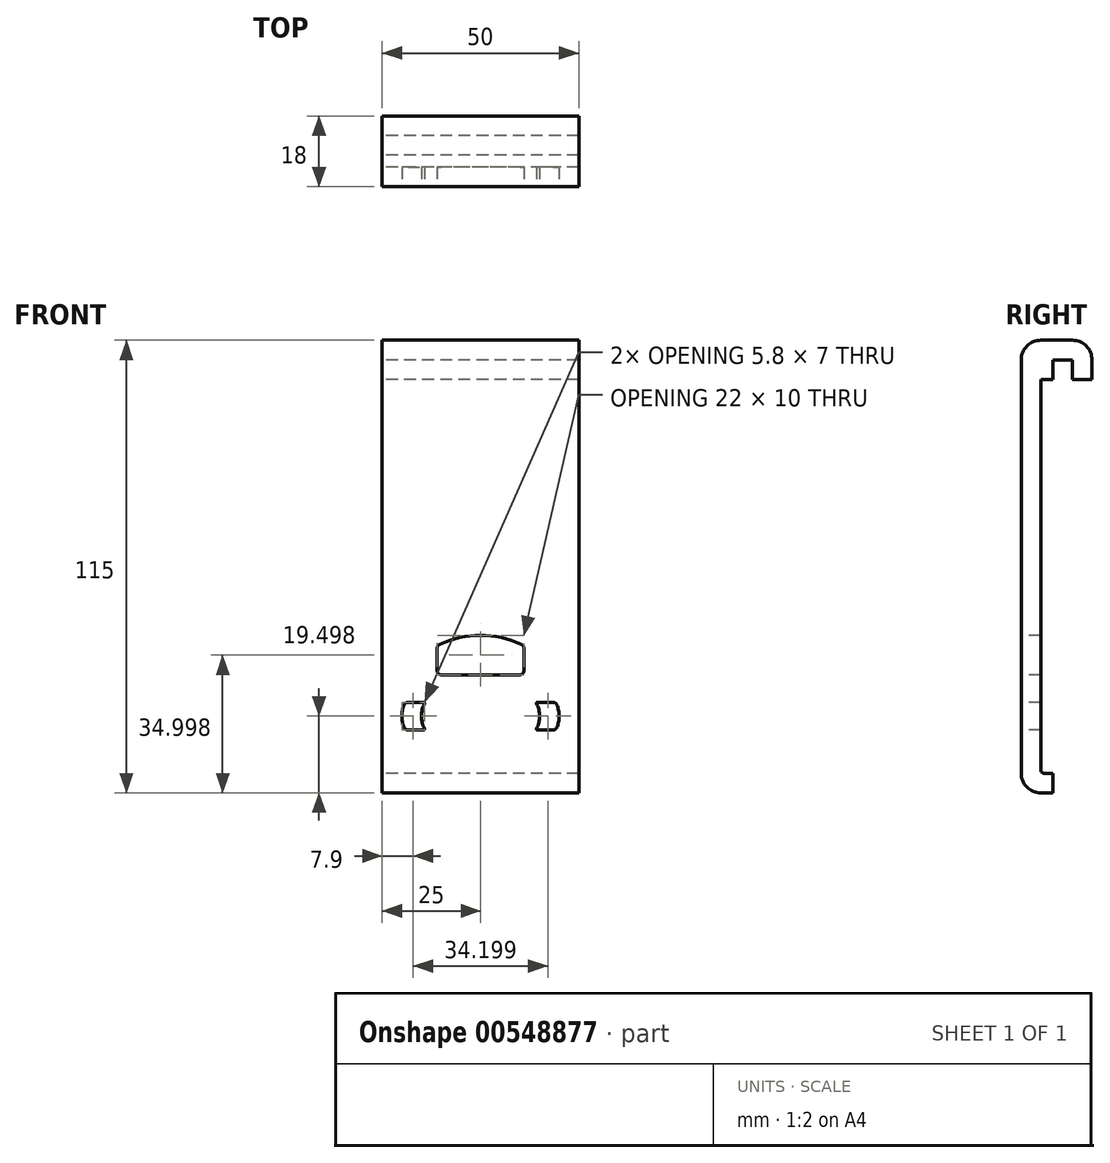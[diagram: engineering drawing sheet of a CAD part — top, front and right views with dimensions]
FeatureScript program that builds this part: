
annotation { "Feature Type Name" : "Feature", "Feature Type Description" : "" }
export const myFeature = defineFeature(function(context is Context, id is Id, definition is map)
    precondition{}
    {
        {
            var Q0;
            Q0=qCreatedBy(makeId("Right.planeOp"),FACE);
            var sketch = newSketch(context, id + "F0", { "sketchPlane" : qUnion([Q0])});
            skLineSegment(sketch, "E0", {"start": v(-5, 54.6) * mm, "end": v(-5, -50.4) * mm});
            skLineSegment(sketch, "E1", {"start": v(0, -55.4) * mm, "end": v(3, -55.4) * mm});
            skLineSegment(sketch, "E2", {"start": v(3, -55.4) * mm, "end": v(3, -50.4) * mm});
            skLineSegment(sketch, "E3", {"start": v(3, -50.4) * mm, "end": v(0.78, -50.4) * mm});
            skLineSegment(sketch, "E4", {"start": v(8, 54.6) * mm, "end": v(8, 49.6) * mm});
            skLineSegment(sketch, "E5", {"start": v(8, 49.6) * mm, "end": v(13, 49.6) * mm});
            skLineSegment(sketch, "E6", {"start": v(13, 49.6) * mm, "end": v(13, 54.6) * mm});
            skLineSegment(sketch, "E7", {"start": v(8, 59.6) * mm, "end": v(0, 59.6) * mm});
            skLineSegment(sketch, "E8", {"start": v(0, -49.6) * mm, "end": v(0, 49.6) * mm});
            skLineSegment(sketch, "E9", {"start": v(0, 49.6) * mm, "end": v(3, 49.6) * mm});
            skLineSegment(sketch, "E10", {"start": v(3, 49.6) * mm, "end": v(3, 54.6) * mm});
            skLineSegment(sketch, "E11", {"start": v(3, 54.6) * mm, "end": v(8, 54.6) * mm});
            skPoint(sketch, "E12.visualSharp", {"position": v(-5, 59.6) * mm});
            skArc(sketch, "E12.filletArc", {"start": v(0, 59.6) * mm, "mid": v(-3.54, 58.14) * mm, "end": v(-5, 54.6) * mm});
            skPoint(sketch, "E13.visualSharp", {"position": v(-5, -55.4) * mm});
            skArc(sketch, "E13.filletArc", {"start": v(-5, -50.4) * mm, "mid": v(-3.54, -53.93) * mm, "end": v(0, -55.4) * mm});
            skPoint(sketch, "E14.visualSharp", {"position": v(13, 59.6) * mm});
            skArc(sketch, "E14.filletArc", {"start": v(13, 54.6) * mm, "mid": v(11.54, 58.14) * mm, "end": v(8, 59.6) * mm});
            skArc(sketch, "E15.filletArc", {"start": v(0, -49.6) * mm, "mid": v(0.23, -50.16) * mm, "end": v(0.78, -50.4) * mm});
            skSolve(sketch);
        }
        {
            var Q0;
            Q0 = qSketchRegion(id + "F0", true);
            extrude(context, id + "F1", {"entities" : qUnion([Q0]), "endBound" : BoundingType.SYMMETRIC, "depth" : 50 * mm, "offsetDistance" : 25 * mm});
        }
        {
            var Q0;
            Q0=makeQuery(id+"F1.opExtrude","SWEPT_FACE",FACE,{"disambiguationData":[OSD([sQuery(id+"F0.wireOp",EDGE,"E0")])]});
            var sketch = newSketch(context, id + "F2", { "sketchPlane" : qUnion([Q0])});
            skLineSegment(sketch, "E16", {"start": v(-10, -25.4) * mm, "end": v(10, -25.4) * mm});
            skLineSegment(sketch, "E17", {"start": v(11, -24.4) * mm, "end": v(11, -18.57) * mm});
            skArc(sketch, "E18", {"start": v(10.42, -17.67) * mm, "mid": v(0, -15.4) * mm, "end": v(-10.42, -17.67) * mm});
            skLineSegment(sketch, "E19", {"start": v(-11, -24.4) * mm, "end": v(-11, -18.57) * mm});
            skPoint(sketch, "E20.visualSharp", {"position": v(11, -25.4) * mm});
            skArc(sketch, "E20.filletArc", {"start": v(10, -25.4) * mm, "mid": v(10.7, -25.1) * mm, "end": v(11, -24.4) * mm});
            skPoint(sketch, "E21.visualSharp", {"position": v(-11, -25.4) * mm});
            skArc(sketch, "E21.filletArc", {"start": v(-11, -24.4) * mm, "mid": v(-10.7, -25.1) * mm, "end": v(-10, -25.4) * mm});
            skPoint(sketch, "E22.visualSharp", {"position": v(-11, -17.94) * mm});
            skArc(sketch, "E22.filletArc", {"start": v(-10.42, -17.67) * mm, "mid": v(-10.84, -18.03) * mm, "end": v(-11, -18.57) * mm});
            skPoint(sketch, "E23.visualSharp", {"position": v(11, -17.94) * mm});
            skArc(sketch, "E23.filletArc", {"start": v(11, -18.57) * mm, "mid": v(10.84, -18.03) * mm, "end": v(10.42, -17.67) * mm});
            skLineSegment(sketch, "E24", {"start": v(14.4, -39.4) * mm, "end": v(18.45, -39.4) * mm});
            skLineSegment(sketch, "E25", {"start": v(14.4, -32.4) * mm, "end": v(18.45, -32.4) * mm});
            skArc(sketch, "E26", {"start": v(19.36, -38.8) * mm, "mid": v(20, -35.9) * mm, "end": v(19.36, -32.98) * mm});
            skArc(sketch, "E27", {"start": v(14.22, -39.1) * mm, "mid": v(15, -35.9) * mm, "end": v(14.22, -32.68) * mm});
            skArc(sketch, "E28.MirrorCS", {"start": v(-14.22, -39.1) * mm, "mid": v(-15, -35.9) * mm, "end": v(-14.22, -32.68) * mm});
            skLineSegment(sketch, "E29.MirrorCS", {"start": v(-14.4, -32.4) * mm, "end": v(-18.45, -32.4) * mm});
            skArc(sketch, "E30.MirrorCS", {"start": v(-19.36, -38.8) * mm, "mid": v(-20, -35.9) * mm, "end": v(-19.36, -32.98) * mm});
            skLineSegment(sketch, "E31.MirrorCS", {"start": v(-14.4, -39.4) * mm, "end": v(-18.45, -39.4) * mm});
            skArc(sketch, "E32.MirrorCS", {"start": v(-14.06, -39.4) * mm, "mid": v(-15, -35.9) * mm, "end": v(-14.06, -32.4) * mm});
            skPoint(sketch, "E33.visualSharp", {"position": v(14.06, -32.4) * mm});
            skArc(sketch, "E33.filletArc", {"start": v(14.4, -32.4) * mm, "mid": v(14.23, -32.49) * mm, "end": v(14.22, -32.68) * mm});
            skPoint(sketch, "E34.visualSharp", {"position": v(14.06, -39.4) * mm});
            skArc(sketch, "E34.filletArc", {"start": v(14.22, -39.1) * mm, "mid": v(14.23, -39.3) * mm, "end": v(14.4, -39.4) * mm});
            skPoint(sketch, "E35.visualSharp", {"position": v(19.06, -39.4) * mm});
            skArc(sketch, "E35.filletArc", {"start": v(18.45, -39.4) * mm, "mid": v(19, -39.23) * mm, "end": v(19.36, -38.8) * mm});
            skPoint(sketch, "E36.visualSharp", {"position": v(19.06, -32.4) * mm});
            skArc(sketch, "E36.filletArc", {"start": v(19.36, -32.98) * mm, "mid": v(19, -32.55) * mm, "end": v(18.45, -32.4) * mm});
            skPoint(sketch, "E37.visualSharp", {"position": v(-19.06, -32.4) * mm});
            skArc(sketch, "E37.filletArc", {"start": v(-18.45, -32.4) * mm, "mid": v(-19, -32.55) * mm, "end": v(-19.36, -32.98) * mm});
            skPoint(sketch, "E38.visualSharp", {"position": v(-19.06, -39.4) * mm});
            skArc(sketch, "E38.filletArc", {"start": v(-19.36, -38.8) * mm, "mid": v(-19, -39.23) * mm, "end": v(-18.45, -39.4) * mm});
            skPoint(sketch, "E39.visualSharp", {"position": v(-14.06, -39.4) * mm});
            skArc(sketch, "E39.filletArc", {"start": v(-14.4, -39.4) * mm, "mid": v(-14.23, -39.3) * mm, "end": v(-14.22, -39.1) * mm});
            skPoint(sketch, "E40.visualSharp", {"position": v(-14.06, -32.4) * mm});
            skArc(sketch, "E40.filletArc", {"start": v(-14.22, -32.68) * mm, "mid": v(-14.23, -32.49) * mm, "end": v(-14.4, -32.4) * mm});
            skSolve(sketch);
        }
        {
            var Q0;
            Q0 = qSketchRegion(id + "F2", true);
            extrude(context, id + "F3", {"entities" : qUnion([Q0]), "operationType" : NewBodyOperationType.REMOVE, "endBound" : BoundingType.UP_TO_NEXT, "oppositeDirection" : true, "depth" : 25 * mm, "offsetDistance" : 25 * mm});
        }
    });
